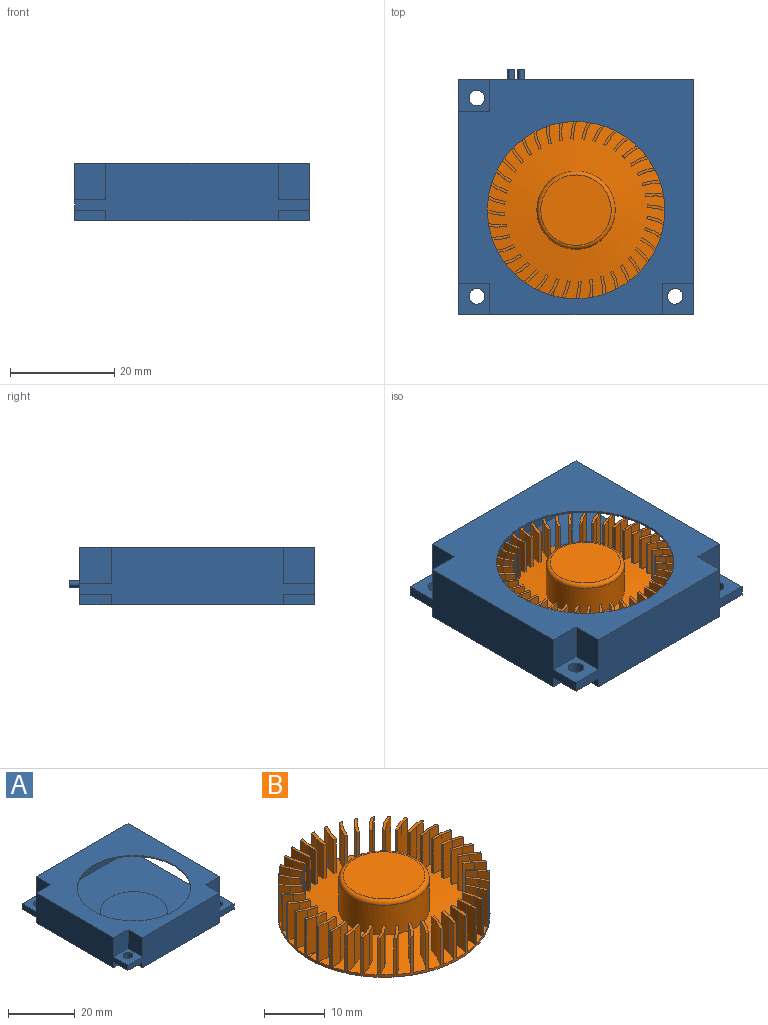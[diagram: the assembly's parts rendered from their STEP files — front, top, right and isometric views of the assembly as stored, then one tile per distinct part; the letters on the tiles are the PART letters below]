
ASSEMBLY  parts=2 mates=1
PART A: 39 faces, bbox 45x47x11 mm
  f0: plane 6x2mm, normal (1,0,0), area 12mm2, adj f1,f8,f17,f26
  f1: plane 6x2mm, normal (0,-1,0), area 12mm2, adj f0,f11,f17,f26
  f2: plane 7x6mm, normal (0,-1,0), area 42mm2, adj f7,f15,f16,f22
  f3: plane 6x2mm, normal (-1,0,0), area 12mm2, adj f6,f8,f17,f23
  f4: plane 7x6mm, normal (-1,0,0), area 42mm2, adj f12,f14,f16,f19
  f5: plane 6x2mm, normal (0,1,0), area 12mm2, adj f13,f15,f17,f20
  f6: plane 6x2mm, normal (0,-1,0), area 12mm2, adj f3,f15,f17,f23
  f7: plane 7x6mm, normal (-1,0,0), area 42mm2, adj f2,f8,f16,f22
  f8: plane 45x11mm, normal (0,-1,0), area 387mm2, adj f0,f3,f7,f9,f11,f15,f16,f17
  f9: plane 7x6mm, normal (1,0,0), area 42mm2, adj f8,f10,f16,f25
  f10: plane 7x6mm, normal (0,-1,0), area 42mm2, adj f9,f11,f16,f25
  f11: plane 45x11mm, normal (1,0,0), area 108mm2, adj f1,f8,f10,f12,f16,f17,f25,f26
  f12: plane 45x11mm, normal (0,1,0), area 438.5mm2, adj f4,f11,f13,f15,f16,f17,f19,f20
  f13: plane 6x2mm, normal (-1,0,0), area 12mm2, adj f5,f12,f17,f20
  f14: plane 7x6mm, normal (0,1,0), area 42mm2, adj f4,f15,f16,f19
  f15: plane 45x11mm, normal (-1,0,0), area 387mm2, adj f2,f5,f6,f8,f12,f14,f16,f17
  f16: plane 45x45mm, normal (0,0,1), area 1009.1mm2, adj f2,f4,f7,f8,f9,f10,f11,f12
  f17: plane 45x45mm, normal (0,0,-1), area 1917mm2, adj f0,f1,f3,f5,f6,f8,f11,f12
  f18: cylinder r=1.5mm len=3mm, axis (0,0,-1), area 18.8mm2, adj f19,f20
  f19: plane 6x6mm, normal (0,0,1), area 28.9mm2, adj f4,f12,f14,f15,f18
  f20: plane 6x6mm, normal (0,0,-1), area 28.9mm2, adj f5,f12,f13,f15,f18
  f21: cylinder r=1.5mm len=3mm, axis (0,0,-1), area 18.8mm2, adj f22,f23
  f22: plane 6x6mm, normal (0,0,1), area 28.9mm2, adj f2,f7,f8,f15,f21
  f23: plane 6x6mm, normal (0,0,-1), area 28.9mm2, adj f3,f6,f8,f15,f21
  f24: cylinder r=1.5mm len=3mm, axis (0,0,-1), area 18.8mm2, adj f25,f26
  f25: plane 6x6mm, normal (0,0,1), area 28.9mm2, adj f8,f9,f10,f11,f24
  f26: plane 6x6mm, normal (0,0,-1), area 28.9mm2, adj f0,f1,f8,f11,f24
  f27: plane 22.5x9mm, normal (0,-1,0), area 202.5mm2, adj f11,f28,f30,f31
  f28: cylinder r=21.5mm len=43mm, axis (0,0,-1), area 756.1mm2, adj f27,f29,f30,f31
  f29: plane 9x7.6mm, normal (0,1,0), area 68.4mm2, adj f11,f28,f30,f31
  f30: plane 44x43mm, normal (0,0,-1), area 712.2mm2, adj f11,f27,f28,f29,f32
  f31: plane 44x43mm, normal (0,0,1), area 1305.9mm2, adj f11,f27,f28,f29,f33
  f32: cylinder r=17mm len=34mm, axis (0,0,1), area 37.4mm2, adj f16,f30
  f33: cylinder r=10mm len=20mm, axis (0,0,-1), area 62.8mm2, adj f31,f34
  f34: plane 20x20mm, normal (0,0,1), area 314.2mm2, adj f33
  f35: cylinder r=0.62mm len=2mm, axis (0,-1,0), area 7.9mm2, adj f12,f36
  f36: plane 1.25x1.25mm, normal (0,1,0), area 1.2mm2, adj f35
  f37: cylinder r=0.62mm len=2mm, axis (0,-1,0), area 7.9mm2, adj f12,f38
  f38: plane 1.25x1.25mm, normal (0,1,0), area 1.2mm2, adj f37
PART B: 247 faces, bbox 35x35x8.3 mm
  f0: cylinder r=17.5mm len=35mm, axis (0,0,-1), area 203.6mm2, adj f1,f4,f5,f8,f9,f12,f14,f15
  f1: plane 35x35mm, normal (0,0,-1), area 962.1mm2, adj f0
  f2: cylinder r=7.5mm len=15mm, axis (0,0,-1), area 282.7mm2, adj f4,f6
  f3: plane 13.5x13.5mm, normal (0,0,1), area 143.1mm2, adj f6
  f4: cone r=7.5mm half-angle=84.3deg, axis (0,0,-1), area 710.3mm2, adj f0,f2,f5,f7,f8,f9,f10,f11
  f5: cone r=7.5mm half-angle=84.3deg, axis (0,0,-1), area 0.5mm2, adj f0,f4,f134
  f6: torus R=6.75mm, axis (0,0,1), area 53.5mm2, adj f2,f3
  f7: plane 7.09x2.02mm, normal (0,1,0), area 13.9mm2, adj f4,f8,f11,f12
  f8: plane 7.28x1.9mm, normal (0.17,0.99,0), area 13.6mm2, adj f0,f4,f7,f12
  f9: plane 7.28x1.96mm, normal (-0.17,-0.99,0), area 14mm2, adj f0,f4,f10,f12
  f10: plane 7.08x2.02mm, normal (0,-1,0), area 13.9mm2, adj f4,f9,f11,f12
  f11: plane 6.88x0.5mm, normal (-1,0,0), area 3.4mm2, adj f4,f7,f10,f12
  f12: plane 3.92x0.84mm, normal (0,0,1), area 1.9mm2, adj f0,f7,f8,f9,f10,f11
  f13: plane 7.09x2mm, normal (0.16,0.99,0), area 13.9mm2, adj f4,f14,f17,f18
  f14: plane 7.28x1.83mm, normal (0.32,0.95,0), area 13.6mm2, adj f0,f4,f13,f18
  f15: plane 7.28x1.88mm, normal (-0.32,-0.95,0), area 14mm2, adj f0,f4,f16,f18
  f16: plane 7.08x1.99mm, normal (-0.16,-0.99,0), area 13.9mm2, adj f4,f15,f17,f18
  f17: plane 6.88x0.5mm, normal (-0.99,0.16,0), area 3.4mm2, adj f4,f13,f16,f18
  f18: plane 3.85x1.44mm, normal (0,0,1), area 1.9mm2, adj f0,f13,f14,f15,f16,f17
  f19: plane 7.09x1.92mm, normal (0.31,0.95,0), area 13.9mm2, adj f4,f20,f23,f24
  f20: plane 7.28x1.71mm, normal (0.47,0.88,0), area 13.6mm2, adj f0,f4,f19,f24
  f21: plane 7.28x1.76mm, normal (-0.47,-0.88,0), area 14mm2, adj f0,f4,f22,f24
  f22: plane 7.08x1.92mm, normal (-0.31,-0.95,0), area 13.9mm2, adj f4,f21,f23,f24
  f23: plane 6.88x0.48mm, normal (-0.95,0.31,0), area 3.4mm2, adj f4,f19,f22,f24
  f24: plane 3.73x2.01mm, normal (0,0,1), area 1.9mm2, adj f0,f19,f20,f21,f22,f23
  f25: plane 7.09x1.8mm, normal (0.45,0.89,0), area 13.9mm2, adj f4,f26,f29,f30
  f26: plane 7.28x1.55mm, normal (0.6,0.8,0), area 13.6mm2, adj f0,f4,f25,f30
  f27: plane 7.28x1.59mm, normal (-0.6,-0.8,0), area 14mm2, adj f0,f4,f28,f30
  f28: plane 7.08x1.8mm, normal (-0.45,-0.89,0), area 13.9mm2, adj f4,f27,f29,f30
  f29: plane 6.88x0.45mm, normal (-0.89,0.45,0), area 3.4mm2, adj f4,f25,f28,f30
  f30: plane 3.53x2.53mm, normal (0,0,1), area 1.9mm2, adj f0,f25,f26,f27,f28,f29
  f31: plane 7.09x1.64mm, normal (0.59,0.81,0), area 13.9mm2, adj f4,f32,f35,f36
  f32: plane 7.28x1.39mm, normal (0.72,0.7,0), area 13.6mm2, adj f0,f4,f31,f36
  f33: plane 7.28x1.43mm, normal (-0.72,-0.7,0), area 14mm2, adj f0,f4,f34,f36
  f34: plane 7.08x1.64mm, normal (-0.59,-0.81,0), area 13.9mm2, adj f4,f33,f35,f36
  f35: plane 6.88x0.41mm, normal (-0.81,0.59,0), area 3.4mm2, adj f4,f31,f34,f36
  f36: plane 3.23x2.98mm, normal (0,0,1), area 1.9mm2, adj f0,f31,f32,f33,f34,f35
  f37: plane 7.09x1.44mm, normal (0.71,0.71,0), area 13.9mm2, adj f4,f38,f41,f42
  f38: plane 7.28x1.58mm, normal (0.82,0.58,0), area 13.6mm2, adj f0,f4,f37,f42
  f39: plane 7.28x1.63mm, normal (-0.82,-0.58,0), area 14mm2, adj f0,f4,f40,f42
  f40: plane 7.08x1.43mm, normal (-0.71,-0.71,0), area 13.9mm2, adj f4,f39,f41,f42
  f41: plane 6.88x0.36mm, normal (-0.71,0.71,0), area 3.4mm2, adj f4,f37,f40,f42
  f42: plane 3.37x2.86mm, normal (0,0,1), area 1.9mm2, adj f0,f37,f38,f39,f40,f41
  f43: plane 7.09x1.64mm, normal (0.81,0.59,0), area 13.9mm2, adj f4,f44,f47,f48
  f44: plane 7.28x1.74mm, normal (0.9,0.44,0), area 13.6mm2, adj f0,f4,f43,f48
  f45: plane 7.28x1.79mm, normal (-0.9,-0.44,0), area 14mm2, adj f0,f4,f46,f48
  f46: plane 7.08x1.64mm, normal (-0.81,-0.59,0), area 13.9mm2, adj f4,f45,f47,f48
  f47: plane 6.88x0.41mm, normal (-0.59,0.81,0), area 3.4mm2, adj f4,f43,f46,f48
  f48: plane 3.67x2.42mm, normal (0,0,1), area 1.9mm2, adj f0,f43,f44,f45,f46,f47
  f49: plane 7.09x1.8mm, normal (0.89,0.45,0), area 13.9mm2, adj f4,f50,f53,f54
  f50: plane 7.28x1.85mm, normal (0.96,0.29,0), area 13.6mm2, adj f0,f4,f49,f54
  f51: plane 7.28x1.9mm, normal (-0.96,-0.29,0), area 14mm2, adj f0,f4,f52,f54
  f52: plane 7.08x1.8mm, normal (-0.89,-0.45,0), area 13.9mm2, adj f4,f51,f53,f54
  f53: plane 6.88x0.45mm, normal (-0.45,0.89,0), area 3.4mm2, adj f4,f49,f52,f54
  f54: plane 3.88x1.91mm, normal (0,0,1), area 1.9mm2, adj f0,f49,f50,f51,f52,f53
  f55: plane 7.09x1.92mm, normal (0.95,0.31,0), area 13.9mm2, adj f4,f56,f59,f60
  f56: plane 7.28x1.91mm, normal (0.99,0.14,0), area 13.6mm2, adj f0,f4,f55,f60
  f57: plane 7.28x1.97mm, normal (-0.99,-0.14,0), area 14mm2, adj f0,f4,f58,f60
  f58: plane 7.08x1.92mm, normal (-0.95,-0.31,0), area 13.9mm2, adj f4,f57,f59,f60
  f59: plane 6.88x0.48mm, normal (-0.31,0.95,0), area 3.4mm2, adj f4,f55,f58,f60
  f60: plane 3.99x1.36mm, normal (0,0,1), area 1.9mm2, adj f0,f55,f56,f57,f58,f59
  f61: plane 7.09x2mm, normal (0.99,0.16,0), area 13.9mm2, adj f4,f62,f65,f66
  f62: plane 7.28x1.93mm, normal (1,-0.02,0), area 13.6mm2, adj f0,f4,f61,f66
  f63: plane 7.28x1.98mm, normal (-1,0.02,0), area 14mm2, adj f0,f4,f64,f66
  f64: plane 7.08x1.99mm, normal (-0.99,-0.16,0), area 13.9mm2, adj f4,f63,f65,f66
  f65: plane 6.88x0.5mm, normal (-0.16,0.99,0), area 3.4mm2, adj f4,f61,f64,f66
  f66: plane 4.01x0.81mm, normal (0,0,1), area 1.9mm2, adj f0,f61,f62,f63,f64,f65
  f67: plane 7.09x2.02mm, normal (1,0,0), area 13.9mm2, adj f4,f68,f71,f72
  f68: plane 7.28x1.9mm, normal (0.99,-0.17,0), area 13.6mm2, adj f0,f4,f67,f72
  f69: plane 7.28x1.96mm, normal (-0.99,0.17,0), area 14mm2, adj f0,f4,f70,f72
  f70: plane 7.08x2.02mm, normal (-1,0,0), area 13.9mm2, adj f4,f69,f71,f72
  f71: plane 6.88x0.5mm, normal (0,1,0), area 3.4mm2, adj f4,f67,f70,f72
  f72: plane 3.92x0.84mm, normal (0,0,1), area 1.9mm2, adj f0,f67,f68,f69,f70,f71
  f73: plane 7.09x2mm, normal (0.99,-0.16,0), area 13.9mm2, adj f4,f74,f77,f78
  f74: plane 7.28x1.83mm, normal (0.95,-0.32,0), area 13.6mm2, adj f0,f4,f73,f78
  f75: plane 7.28x1.88mm, normal (-0.95,0.32,0), area 14mm2, adj f0,f4,f76,f78
  f76: plane 7.08x1.99mm, normal (-0.99,0.16,0), area 13.9mm2, adj f4,f75,f77,f78
  f77: plane 6.88x0.5mm, normal (0.16,0.99,0), area 3.4mm2, adj f4,f73,f76,f78
  f78: plane 3.85x1.44mm, normal (0,0,1), area 1.9mm2, adj f0,f73,f74,f75,f76,f77
  f79: plane 7.09x1.92mm, normal (0.95,-0.31,0), area 13.9mm2, adj f4,f80,f83,f84
  f80: plane 7.28x1.71mm, normal (0.88,-0.47,0), area 13.6mm2, adj f0,f4,f79,f84
  f81: plane 7.28x1.76mm, normal (-0.88,0.47,0), area 14mm2, adj f0,f4,f82,f84
  f82: plane 7.08x1.92mm, normal (-0.95,0.31,0), area 13.9mm2, adj f4,f81,f83,f84
  f83: plane 6.88x0.48mm, normal (0.31,0.95,0), area 3.4mm2, adj f4,f79,f82,f84
  f84: plane 3.73x2.01mm, normal (0,0,1), area 1.9mm2, adj f0,f79,f80,f81,f82,f83
  f85: plane 7.09x1.8mm, normal (0.89,-0.45,0), area 13.9mm2, adj f4,f86,f89,f90
  f86: plane 7.28x1.55mm, normal (0.8,-0.6,0), area 13.6mm2, adj f0,f4,f85,f90
  f87: plane 7.28x1.59mm, normal (-0.8,0.6,0), area 14mm2, adj f0,f4,f88,f90
  f88: plane 7.08x1.8mm, normal (-0.89,0.45,0), area 13.9mm2, adj f4,f87,f89,f90
  f89: plane 6.88x0.45mm, normal (0.45,0.89,0), area 3.4mm2, adj f4,f85,f88,f90
  f90: plane 3.53x2.53mm, normal (0,0,1), area 1.9mm2, adj f0,f85,f86,f87,f88,f89
  f91: plane 7.09x1.64mm, normal (0.81,-0.59,0), area 13.9mm2, adj f4,f92,f95,f96
  f92: plane 7.28x1.39mm, normal (0.7,-0.72,0), area 13.6mm2, adj f0,f4,f91,f96
  f93: plane 7.28x1.43mm, normal (-0.7,0.72,0), area 14mm2, adj f0,f4,f94,f96
  f94: plane 7.08x1.64mm, normal (-0.81,0.59,0), area 13.9mm2, adj f4,f93,f95,f96
  f95: plane 6.88x0.41mm, normal (0.59,0.81,0), area 3.4mm2, adj f4,f91,f94,f96
  f96: plane 3.23x2.98mm, normal (0,0,1), area 1.9mm2, adj f0,f91,f92,f93,f94,f95
  f97: plane 7.09x1.44mm, normal (0.71,-0.71,0), area 13.9mm2, adj f4,f98,f101,f102
  f98: plane 7.28x1.58mm, normal (0.58,-0.82,0), area 13.6mm2, adj f0,f4,f97,f102
  f99: plane 7.28x1.63mm, normal (-0.58,0.82,0), area 14mm2, adj f0,f4,f100,f102
  f100: plane 7.08x1.43mm, normal (-0.71,0.71,0), area 13.9mm2, adj f4,f99,f101,f102
  f101: plane 6.88x0.36mm, normal (0.71,0.71,0), area 3.4mm2, adj f4,f97,f100,f102
  f102: plane 3.37x2.86mm, normal (0,0,1), area 1.9mm2, adj f0,f97,f98,f99,f100,f101
  f103: plane 7.09x1.64mm, normal (0.59,-0.81,0), area 13.9mm2, adj f4,f104,f107,f108
  f104: plane 7.28x1.74mm, normal (0.44,-0.9,0), area 13.6mm2, adj f0,f4,f103,f108
  f105: plane 7.28x1.79mm, normal (-0.44,0.9,0), area 14mm2, adj f0,f4,f106,f108
  f106: plane 7.08x1.64mm, normal (-0.59,0.81,0), area 13.9mm2, adj f4,f105,f107,f108
  f107: plane 6.88x0.41mm, normal (0.81,0.59,0), area 3.4mm2, adj f4,f103,f106,f108
  f108: plane 3.67x2.42mm, normal (0,0,1), area 1.9mm2, adj f0,f103,f104,f105,f106,f107
  f109: plane 7.09x1.8mm, normal (0.45,-0.89,0), area 13.9mm2, adj f4,f110,f113,f114
  f110: plane 7.28x1.85mm, normal (0.29,-0.96,0), area 13.6mm2, adj f0,f4,f109,f114
  f111: plane 7.28x1.9mm, normal (-0.29,0.96,0), area 14mm2, adj f0,f4,f112,f114
  f112: plane 7.08x1.8mm, normal (-0.45,0.89,0), area 13.9mm2, adj f4,f111,f113,f114
  f113: plane 6.88x0.45mm, normal (0.89,0.45,0), area 3.4mm2, adj f4,f109,f112,f114
  f114: plane 3.88x1.91mm, normal (0,0,1), area 1.9mm2, adj f0,f109,f110,f111,f112,f113
  f115: plane 7.09x1.92mm, normal (0.31,-0.95,0), area 13.9mm2, adj f4,f116,f119,f120
  f116: plane 7.28x1.91mm, normal (0.14,-0.99,0), area 13.6mm2, adj f0,f4,f115,f120
  f117: plane 7.28x1.97mm, normal (-0.14,0.99,0), area 14mm2, adj f0,f4,f118,f120
  f118: plane 7.08x1.92mm, normal (-0.31,0.95,0), area 13.9mm2, adj f4,f117,f119,f120
  f119: plane 6.88x0.48mm, normal (0.95,0.31,0), area 3.4mm2, adj f4,f115,f118,f120
  f120: plane 3.99x1.36mm, normal (0,0,1), area 1.9mm2, adj f0,f115,f116,f117,f118,f119
  f121: plane 7.09x2mm, normal (0.16,-0.99,0), area 13.9mm2, adj f4,f122,f125,f126
  f122: plane 7.28x1.93mm, normal (-0.02,-1,0), area 13.6mm2, adj f0,f4,f121,f126
  f123: plane 7.28x1.98mm, normal (0.02,1,0), area 14mm2, adj f0,f4,f124,f126
  f124: plane 7.08x1.99mm, normal (-0.16,0.99,0), area 13.9mm2, adj f4,f123,f125,f126
  f125: plane 6.88x0.5mm, normal (0.99,0.16,0), area 3.4mm2, adj f4,f121,f124,f126
  f126: plane 4.01x0.81mm, normal (0,0,1), area 1.9mm2, adj f0,f121,f122,f123,f124,f125
  f127: plane 7.09x2.02mm, normal (0,-1,0), area 13.9mm2, adj f4,f128,f131,f132
  f128: plane 7.28x1.9mm, normal (-0.17,-0.99,0), area 13.6mm2, adj f0,f4,f127,f132
  f129: plane 7.28x1.96mm, normal (0.17,0.99,0), area 14mm2, adj f0,f4,f130,f132
  f130: plane 7.08x2.02mm, normal (0,1,0), area 13.9mm2, adj f4,f129,f131,f132
  f131: plane 6.88x0.5mm, normal (1,0,0), area 3.4mm2, adj f4,f127,f130,f132
  f132: plane 3.92x0.84mm, normal (0,0,1), area 1.9mm2, adj f0,f127,f128,f129,f130,f131
  f133: plane 7.09x2mm, normal (-0.16,-0.99,0), area 13.9mm2, adj f4,f134,f137,f138
  f134: plane 7.28x1.83mm, normal (-0.32,-0.95,0), area 13.6mm2, adj f0,f5,f133,f138
  f135: plane 7.28x1.88mm, normal (0.32,0.95,0), area 14mm2, adj f0,f4,f136,f138
  f136: plane 7.08x1.99mm, normal (0.16,0.99,0), area 13.9mm2, adj f4,f135,f137,f138
  f137: plane 6.87x0.5mm, normal (0.99,-0.16,0), area 3.4mm2, adj f4,f133,f136,f138
  f138: plane 3.85x1.44mm, normal (0,0,1), area 1.9mm2, adj f0,f133,f134,f135,f136,f137
  f139: plane 7.09x1.92mm, normal (-0.31,-0.95,0), area 13.9mm2, adj f4,f140,f143,f144
  f140: plane 7.28x1.71mm, normal (-0.47,-0.88,0), area 13.6mm2, adj f0,f4,f139,f144
  f141: plane 7.28x1.76mm, normal (0.47,0.88,0), area 14mm2, adj f0,f4,f142,f144
  f142: plane 7.08x1.92mm, normal (0.31,0.95,0), area 13.9mm2, adj f4,f141,f143,f144
  f143: plane 6.88x0.48mm, normal (0.95,-0.31,0), area 3.4mm2, adj f4,f139,f142,f144
  f144: plane 3.73x2.01mm, normal (0,0,1), area 1.9mm2, adj f0,f139,f140,f141,f142,f143
  f145: plane 7.09x1.8mm, normal (-0.45,-0.89,0), area 13.9mm2, adj f4,f146,f149,f150
  f146: plane 7.28x1.55mm, normal (-0.6,-0.8,0), area 13.6mm2, adj f0,f4,f145,f150
  f147: plane 7.28x1.59mm, normal (0.6,0.8,0), area 14mm2, adj f0,f4,f148,f150
  f148: plane 7.08x1.8mm, normal (0.45,0.89,0), area 13.9mm2, adj f4,f147,f149,f150
  f149: plane 6.88x0.45mm, normal (0.89,-0.45,0), area 3.4mm2, adj f4,f145,f148,f150
  f150: plane 3.53x2.53mm, normal (0,0,1), area 1.9mm2, adj f0,f145,f146,f147,f148,f149
  f151: plane 7.09x1.64mm, normal (-0.59,-0.81,0), area 13.9mm2, adj f4,f152,f155,f156
  f152: plane 7.28x1.39mm, normal (-0.72,-0.7,0), area 13.6mm2, adj f0,f4,f151,f156
  f153: plane 7.28x1.43mm, normal (0.72,0.7,0), area 14mm2, adj f0,f4,f154,f156
  f154: plane 7.08x1.64mm, normal (0.59,0.81,0), area 13.9mm2, adj f4,f153,f155,f156
  f155: plane 6.88x0.41mm, normal (0.81,-0.59,0), area 3.4mm2, adj f4,f151,f154,f156
  f156: plane 3.23x2.98mm, normal (0,0,1), area 1.9mm2, adj f0,f151,f152,f153,f154,f155
  f157: plane 7.09x1.44mm, normal (-0.71,-0.71,0), area 13.9mm2, adj f4,f158,f161,f162
  f158: plane 7.28x1.58mm, normal (-0.82,-0.58,0), area 13.6mm2, adj f0,f4,f157,f162
  f159: plane 7.28x1.63mm, normal (0.82,0.58,0), area 14mm2, adj f0,f4,f160,f162
  f160: plane 7.08x1.43mm, normal (0.71,0.71,0), area 13.9mm2, adj f4,f159,f161,f162
  f161: plane 6.88x0.36mm, normal (0.71,-0.71,0), area 3.4mm2, adj f4,f157,f160,f162
  f162: plane 3.37x2.86mm, normal (0,0,1), area 1.9mm2, adj f0,f157,f158,f159,f160,f161
  f163: plane 7.09x1.64mm, normal (-0.81,-0.59,0), area 13.9mm2, adj f4,f164,f167,f168
  f164: plane 7.28x1.74mm, normal (-0.9,-0.44,0), area 13.6mm2, adj f0,f4,f163,f168
  f165: plane 7.28x1.79mm, normal (0.9,0.44,0), area 14mm2, adj f0,f4,f166,f168
  f166: plane 7.08x1.64mm, normal (0.81,0.59,0), area 13.9mm2, adj f4,f165,f167,f168
  f167: plane 6.88x0.41mm, normal (0.59,-0.81,0), area 3.4mm2, adj f4,f163,f166,f168
  f168: plane 3.67x2.42mm, normal (0,0,1), area 1.9mm2, adj f0,f163,f164,f165,f166,f167
  f169: plane 7.09x1.8mm, normal (-0.89,-0.45,0), area 13.9mm2, adj f4,f170,f173,f174
  f170: plane 7.28x1.85mm, normal (-0.96,-0.29,0), area 13.6mm2, adj f0,f4,f169,f174
  f171: plane 7.28x1.9mm, normal (0.96,0.29,0), area 14mm2, adj f0,f4,f172,f174
  f172: plane 7.08x1.8mm, normal (0.89,0.45,0), area 13.9mm2, adj f4,f171,f173,f174
  f173: plane 6.88x0.45mm, normal (0.45,-0.89,0), area 3.4mm2, adj f4,f169,f172,f174
  f174: plane 3.88x1.91mm, normal (0,0,1), area 1.9mm2, adj f0,f169,f170,f171,f172,f173
  f175: plane 7.09x1.92mm, normal (-0.95,-0.31,0), area 13.9mm2, adj f4,f176,f179,f180
  f176: plane 7.28x1.91mm, normal (-0.99,-0.14,0), area 13.6mm2, adj f0,f4,f175,f180
  f177: plane 7.28x1.97mm, normal (0.99,0.14,0), area 14mm2, adj f0,f4,f178,f180
  f178: plane 7.08x1.92mm, normal (0.95,0.31,0), area 13.9mm2, adj f4,f177,f179,f180
  f179: plane 6.88x0.48mm, normal (0.31,-0.95,0), area 3.4mm2, adj f4,f175,f178,f180
  f180: plane 3.99x1.36mm, normal (0,0,1), area 1.9mm2, adj f0,f175,f176,f177,f178,f179
  f181: plane 7.09x2mm, normal (-0.99,-0.16,0), area 13.9mm2, adj f4,f182,f185,f186
  f182: plane 7.28x1.93mm, normal (-1,0.02,0), area 13.6mm2, adj f0,f4,f181,f186
  f183: plane 7.28x1.98mm, normal (1,-0.02,0), area 14mm2, adj f0,f4,f184,f186
  f184: plane 7.08x1.99mm, normal (0.99,0.16,0), area 13.9mm2, adj f4,f183,f185,f186
  f185: plane 6.88x0.5mm, normal (0.16,-0.99,0), area 3.4mm2, adj f4,f181,f184,f186
  f186: plane 4.01x0.81mm, normal (0,0,1), area 1.9mm2, adj f0,f181,f182,f183,f184,f185
  f187: plane 7.09x2.02mm, normal (-1,0,0), area 13.9mm2, adj f4,f188,f191,f192
  f188: plane 7.28x1.9mm, normal (-0.99,0.17,0), area 13.6mm2, adj f0,f4,f187,f192
  f189: plane 7.28x1.96mm, normal (0.99,-0.17,0), area 14mm2, adj f0,f4,f190,f192
  f190: plane 7.08x2.02mm, normal (1,0,0), area 13.9mm2, adj f4,f189,f191,f192
  f191: plane 6.88x0.5mm, normal (0,-1,0), area 3.4mm2, adj f4,f187,f190,f192
  f192: plane 3.92x0.84mm, normal (0,0,1), area 1.9mm2, adj f0,f187,f188,f189,f190,f191
  f193: plane 7.09x2mm, normal (-0.99,0.16,0), area 13.9mm2, adj f4,f194,f197,f198
  f194: plane 7.28x1.83mm, normal (-0.95,0.32,0), area 13.6mm2, adj f0,f4,f193,f198
  f195: plane 7.28x1.88mm, normal (0.95,-0.32,0), area 14mm2, adj f0,f4,f196,f198
  f196: plane 7.08x1.99mm, normal (0.99,-0.16,0), area 13.9mm2, adj f4,f195,f197,f198
  f197: plane 6.88x0.5mm, normal (-0.16,-0.99,0), area 3.4mm2, adj f4,f193,f196,f198
  f198: plane 3.85x1.44mm, normal (0,0,1), area 1.9mm2, adj f0,f193,f194,f195,f196,f197
  f199: plane 7.09x1.92mm, normal (-0.95,0.31,0), area 13.9mm2, adj f4,f200,f203,f204
  f200: plane 7.28x1.71mm, normal (-0.88,0.47,0), area 13.6mm2, adj f0,f4,f199,f204
  f201: plane 7.28x1.76mm, normal (0.88,-0.47,0), area 14mm2, adj f0,f4,f202,f204
  f202: plane 7.08x1.92mm, normal (0.95,-0.31,0), area 13.9mm2, adj f4,f201,f203,f204
  f203: plane 6.88x0.48mm, normal (-0.31,-0.95,0), area 3.4mm2, adj f4,f199,f202,f204
  f204: plane 3.73x2.01mm, normal (0,0,1), area 1.9mm2, adj f0,f199,f200,f201,f202,f203
  f205: plane 7.09x1.8mm, normal (-0.89,0.45,0), area 13.9mm2, adj f4,f206,f209,f210
  f206: plane 7.28x1.55mm, normal (-0.8,0.6,0), area 13.6mm2, adj f0,f4,f205,f210
  f207: plane 7.28x1.59mm, normal (0.8,-0.6,0), area 14mm2, adj f0,f4,f208,f210
  f208: plane 7.08x1.8mm, normal (0.89,-0.45,0), area 13.9mm2, adj f4,f207,f209,f210
  f209: plane 6.88x0.45mm, normal (-0.45,-0.89,0), area 3.4mm2, adj f4,f205,f208,f210
  f210: plane 3.53x2.53mm, normal (0,0,1), area 1.9mm2, adj f0,f205,f206,f207,f208,f209
  f211: plane 7.09x1.64mm, normal (-0.81,0.59,0), area 13.9mm2, adj f4,f212,f215,f216
  f212: plane 7.28x1.39mm, normal (-0.7,0.72,0), area 13.6mm2, adj f0,f4,f211,f216
  f213: plane 7.28x1.43mm, normal (0.7,-0.72,0), area 14mm2, adj f0,f4,f214,f216
  f214: plane 7.08x1.64mm, normal (0.81,-0.59,0), area 13.9mm2, adj f4,f213,f215,f216
  f215: plane 6.88x0.41mm, normal (-0.59,-0.81,0), area 3.4mm2, adj f4,f211,f214,f216
  f216: plane 3.23x2.98mm, normal (0,0,1), area 1.9mm2, adj f0,f211,f212,f213,f214,f215
  f217: plane 7.09x1.44mm, normal (-0.71,0.71,0), area 13.9mm2, adj f4,f218,f221,f222
  f218: plane 7.28x1.58mm, normal (-0.58,0.82,0), area 13.6mm2, adj f0,f4,f217,f222
  f219: plane 7.28x1.63mm, normal (0.58,-0.82,0), area 14mm2, adj f0,f4,f220,f222
  f220: plane 7.08x1.43mm, normal (0.71,-0.71,0), area 13.9mm2, adj f4,f219,f221,f222
  f221: plane 6.88x0.36mm, normal (-0.71,-0.71,0), area 3.4mm2, adj f4,f217,f220,f222
  f222: plane 3.37x2.86mm, normal (0,0,1), area 1.9mm2, adj f0,f217,f218,f219,f220,f221
  f223: plane 7.09x1.64mm, normal (-0.59,0.81,0), area 13.9mm2, adj f4,f224,f227,f228
  f224: plane 7.28x1.74mm, normal (-0.44,0.9,0), area 13.6mm2, adj f0,f4,f223,f228
  f225: plane 7.28x1.79mm, normal (0.44,-0.9,0), area 14mm2, adj f0,f4,f226,f228
  f226: plane 7.08x1.64mm, normal (0.59,-0.81,0), area 13.9mm2, adj f4,f225,f227,f228
  f227: plane 6.88x0.41mm, normal (-0.81,-0.59,0), area 3.4mm2, adj f4,f223,f226,f228
  f228: plane 3.67x2.42mm, normal (0,0,1), area 1.9mm2, adj f0,f223,f224,f225,f226,f227
  f229: plane 7.09x1.8mm, normal (-0.45,0.89,0), area 13.9mm2, adj f4,f230,f233,f234
  f230: plane 7.28x1.85mm, normal (-0.29,0.96,0), area 13.6mm2, adj f0,f4,f229,f234
  f231: plane 7.28x1.9mm, normal (0.29,-0.96,0), area 14mm2, adj f0,f4,f232,f234
  f232: plane 7.08x1.8mm, normal (0.45,-0.89,0), area 13.9mm2, adj f4,f231,f233,f234
  f233: plane 6.88x0.45mm, normal (-0.89,-0.45,0), area 3.4mm2, adj f4,f229,f232,f234
  f234: plane 3.88x1.91mm, normal (0,0,1), area 1.9mm2, adj f0,f229,f230,f231,f232,f233
  f235: plane 7.09x1.92mm, normal (-0.31,0.95,0), area 13.9mm2, adj f4,f236,f239,f240
  f236: plane 7.28x1.91mm, normal (-0.14,0.99,0), area 13.6mm2, adj f0,f4,f235,f240
  f237: plane 7.28x1.97mm, normal (0.14,-0.99,0), area 14mm2, adj f0,f4,f238,f240
  f238: plane 7.08x1.92mm, normal (0.31,-0.95,0), area 13.9mm2, adj f4,f237,f239,f240
  f239: plane 6.88x0.48mm, normal (-0.95,-0.31,0), area 3.4mm2, adj f4,f235,f238,f240
  f240: plane 3.99x1.36mm, normal (0,0,1), area 1.9mm2, adj f0,f235,f236,f237,f238,f239
  f241: plane 7.09x2mm, normal (-0.16,0.99,0), area 13.9mm2, adj f4,f242,f245,f246
  f242: plane 7.28x1.93mm, normal (0.02,1,0), area 13.6mm2, adj f0,f4,f241,f246
  f243: plane 7.28x1.98mm, normal (-0.02,-1,0), area 14mm2, adj f0,f4,f244,f246
  f244: plane 7.08x1.99mm, normal (0.16,-0.99,0), area 13.9mm2, adj f4,f243,f245,f246
  f245: plane 6.88x0.5mm, normal (-0.99,-0.16,0), area 3.4mm2, adj f4,f241,f244,f246
  f246: plane 4.01x0.81mm, normal (0,0,1), area 1.9mm2, adj f0,f241,f242,f243,f244,f245
PLACE A t=(-2.1,-5.72,-3.78)mm fixed
PLACE B rot(axis=(0,0,1),74.9deg) t=(-2.1,-5.72,-3.78)mm
MATE revolute B.f0 <-> A.f32  axis (0,0,-1) through (-2.1,-5.72,-1.13)mm
